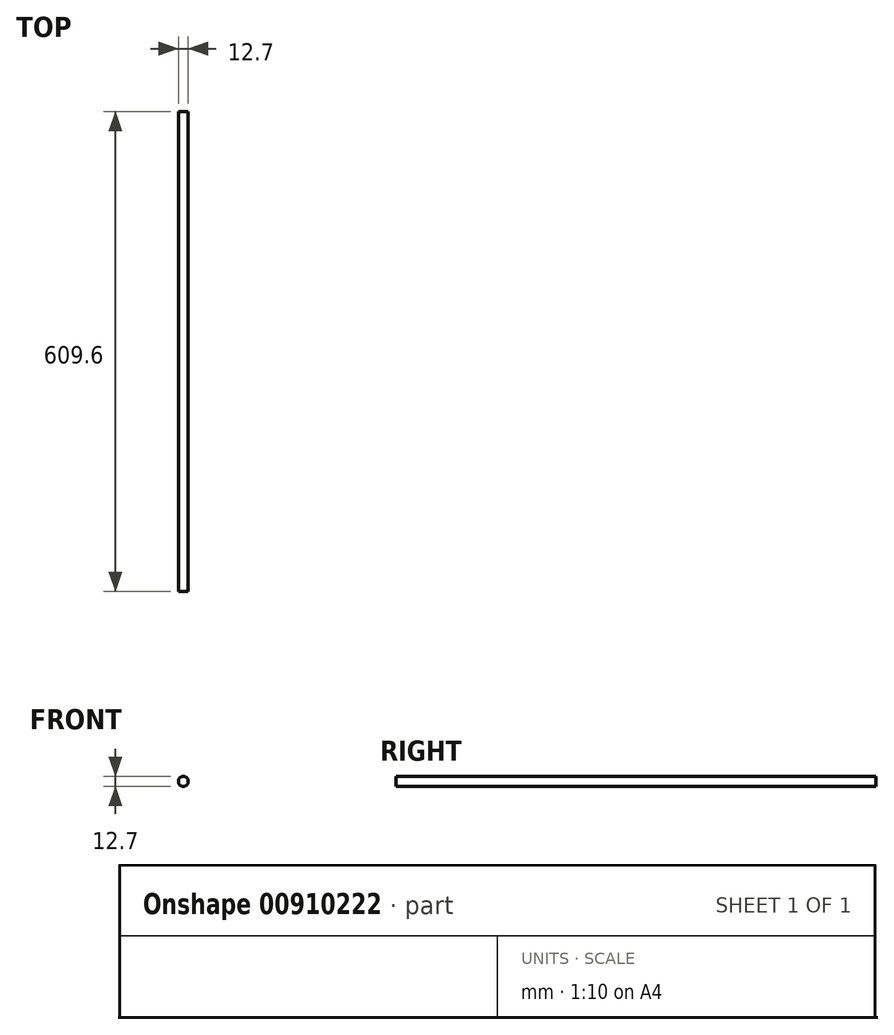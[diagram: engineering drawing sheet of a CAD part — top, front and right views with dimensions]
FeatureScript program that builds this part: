
annotation { "Feature Type Name" : "Feature", "Feature Type Description" : "" }
export const myFeature = defineFeature(function(context is Context, id is Id, definition is map)
    precondition{}
    {
        {
            var Q0;
            Q0=qCreatedBy(makeId("Front.planeOp"),FACE);
            var sketch = newSketch(context, id + "F0", { "sketchPlane" : qUnion([Q0])});
            skCircle(sketch, "E0", {"center": v(0, 0) * mm, "radius": 6.35 * mm});
            skSolve(sketch);
        }
        {
            var Q0;
            Q0 = qSketchRegion(id + "F0", true);
            extrude(context, id + "F1", {"entities" : qUnion([Q0]), "depth" : 609.6 * mm, "offsetDistance" : 25.4 * mm});
        }
    });
